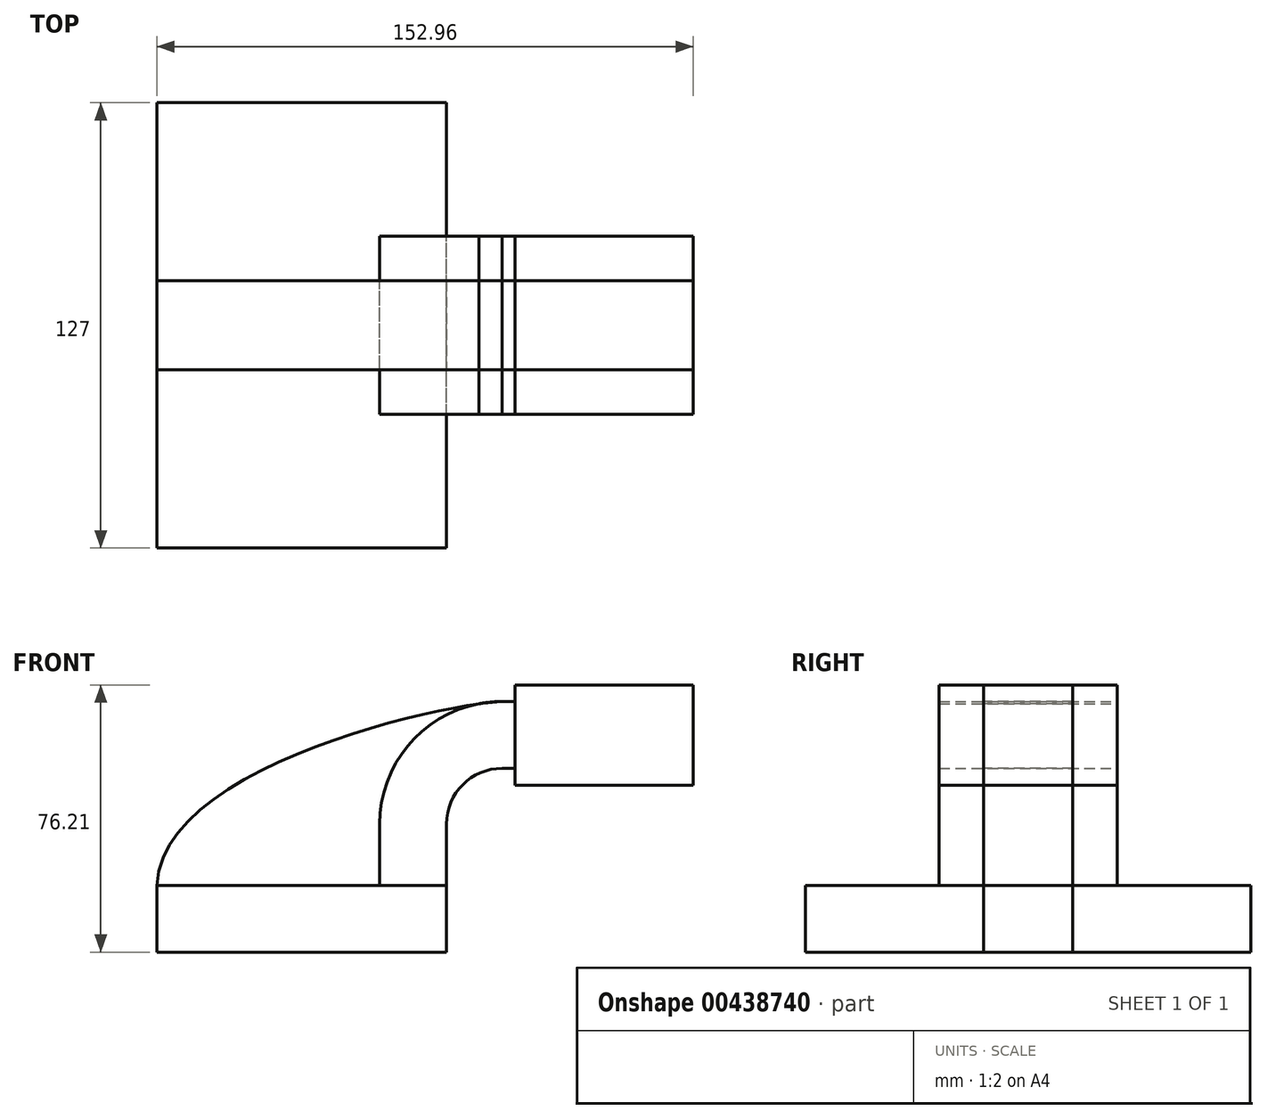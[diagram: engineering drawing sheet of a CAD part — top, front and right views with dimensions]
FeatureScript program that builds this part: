
annotation { "Feature Type Name" : "Feature", "Feature Type Description" : "" }
export const myFeature = defineFeature(function(context is Context, id is Id, definition is map)
    precondition{}
    {
        {
            var Q0;
            Q0=qCreatedBy(makeId("Front.planeOp"),FACE);
            var sketch = newSketch(context, id + "F0", { "sketchPlane" : qUnion([Q0])});
            skLineSegment(sketch, "E0.bottom", {"start": v(41.27, 9.53) * mm, "end": v(-41.28, 9.53) * mm});
            skLineSegment(sketch, "E0.top", {"start": v(41.28, -9.52) * mm, "end": v(-41.27, -9.52) * mm});
            skLineSegment(sketch, "E0.left", {"start": v(41.28, 9.53) * mm, "end": v(41.28, -9.52) * mm});
            skLineSegment(sketch, "E0.right", {"start": v(-41.28, 9.53) * mm, "end": v(-41.27, -9.52) * mm});
            skPoint(sketch, "E0.middle", {"position": v(0, 0) * mm});
            skLineSegment(sketch, "E1.bottom", {"start": v(60.88, 66.68) * mm, "end": v(111.68, 66.68) * mm});
            skLineSegment(sketch, "E1.top", {"start": v(60.88, 38.1) * mm, "end": v(111.68, 38.1) * mm});
            skLineSegment(sketch, "E1.left", {"start": v(60.88, 66.68) * mm, "end": v(60.88, 38.1) * mm});
            skLineSegment(sketch, "E1.right", {"start": v(111.68, 66.68) * mm, "end": v(111.68, 38.1) * mm});
            skPoint(sketch, "E1.middle", {"position": v(86.28, 52.39) * mm});
            skLineSegment(sketch, "E2", {"start": v(41.27, 9.53) * mm, "end": v(41.27, 27) * mm});
            skArc(sketch, "E3", {"start": v(41.27, 27) * mm, "mid": v(45.92, 38.23) * mm, "end": v(57.15, 42.88) * mm});
            skLineSegment(sketch, "E4", {"start": v(57.15, 42.88) * mm, "end": v(60.88, 42.88) * mm});
            skLineSegment(sketch, "E5.0", {"start": v(57.15, 61.93) * mm, "end": v(60.88, 61.93) * mm});
            skArc(sketch, "E5.1", {"start": v(22.23, 27) * mm, "mid": v(32.45, 51.7) * mm, "end": v(57.15, 61.93) * mm});
            skLineSegment(sketch, "E5.2", {"start": v(22.22, 9.53) * mm, "end": v(22.22, 27) * mm});
            skLineSegment(sketch, "E6", {"start": v(60.88, 61.93) * mm, "end": v(60.88, 42.88) * mm});
            skFitSpline(sketch, "E7", {"points": [v(-41.28, 9.52) * mm, v(57.15, 61.93) * mm], "startDerivative": vector(4.22, 103.93) * mm, "endDerivative": vector(44.68, 0.78) * mm});
            skSolve(sketch);
        }
        {
            var Q0;
            Q0=makeQuery(id+"F0.imprint","IMPRINT",FACE,{"disambiguationData":[TD([[makeQuery(id+"F0.imprint","IMPRINT",EDGE,{"derivedFrom":sQuery(id+"F0.wireOp",EDGE,"E0.top")}),-1.0]])]});
            extrude(context, id + "F1", {"entities" : qUnion([Q0]), "endBound" : BoundingType.SYMMETRIC, "depth" : 127 * mm});
        }
        {
            var Q0;
            {var subQ3=sQuery(id+"F0.wireOp",EDGE,"E1.bottom");Q0=makeQuery(id+"F0.imprint","IMPRINT",FACE,{"disambiguationData":[TD([[makeQuery(id+"F0.imprint","IMPRINT",EDGE,{"derivedFrom":subQ3}),-1.0]])]});}
            extrude(context, id + "F2", {"entities" : qUnion([Q0]), "operationType" : NewBodyOperationType.ADD, "endBound" : BoundingType.SYMMETRIC, "depth" : 50.8 * mm});
        }
        {
            var Q0;
            Q0 = qSketchRegion(id + "F0", true);
            extrude(context, id + "F3", {"entities" : qUnion([Q0]), "endBound" : BoundingType.SYMMETRIC, "oppositeDirection" : true, "depth" : 25.4 * mm});
        }
        {
            var Q0;
            {var subQ0=sQuery(id+"F0.wireOp",EDGE,"E2");Q0=makeQuery(id+"F0.imprint","IMPRINT",FACE,{"disambiguationData":[TD([[makeQuery(id+"F0.imprint","IMPRINT",EDGE,{"derivedFrom":subQ0}),1.0]])]});}
            extrude(context, id + "F4", {"entities" : qUnion([Q0]), "endBound" : BoundingType.SYMMETRIC, "depth" : 50.8 * mm});
        }
    });
